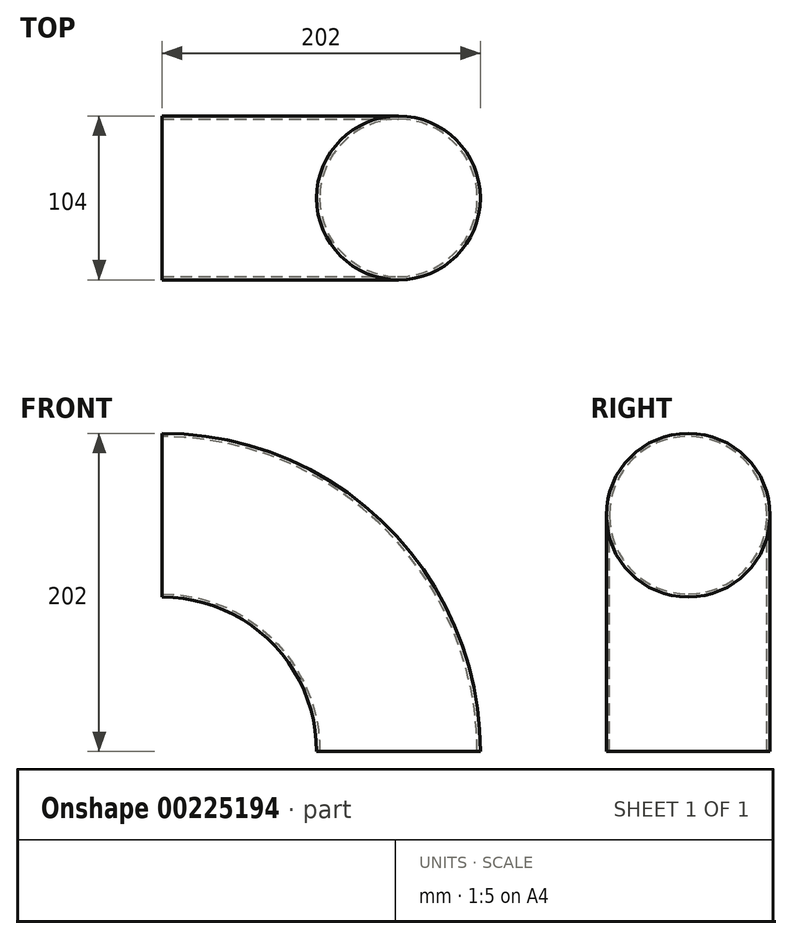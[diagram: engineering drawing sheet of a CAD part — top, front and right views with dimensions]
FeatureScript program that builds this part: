
annotation { "Feature Type Name" : "Feature", "Feature Type Description" : "" }
export const myFeature = defineFeature(function(context is Context, id is Id, definition is map)
    precondition{}
    {
        {
            var Q0;
            Q0=qCreatedBy(makeId("Right.planeOp"),FACE);
            var sketch = newSketch(context, id + "F0", { "sketchPlane" : qUnion([Q0])});
            skCircle(sketch, "E0", {"center": v(0, 0) * mm, "radius": 52 * mm});
            skCircle(sketch, "E1", {"center": v(0, 0) * mm, "radius": 50 * mm});
            skSolve(sketch);
        }
        {
            var Q0;
            Q0=qCreatedBy(makeId("Front.planeOp"),FACE);
            var sketch = newSketch(context, id + "F1", { "sketchPlane" : qUnion([Q0])});
            skLineSegment(sketch, "E2", {"start": v(0, 0) * mm, "end": v(0, 0) * mm});
            skLineSegment(sketch, "E3", {"start": v(150, -150) * mm, "end": v(150, -150) * mm});
            skPoint(sketch, "E4.visualSharp", {"position": v(150, 0) * mm});
            skArc(sketch, "E4.filletArc", {"start": v(150, -150) * mm, "mid": v(106.07, -43.93) * mm, "end": v(0, 0) * mm});
            skSolve(sketch);
        }
        {
            var Q0;
            Q0=makeQuery(id+"F0.imprint","IMPRINT",FACE,{"disambiguationData":[TD([[makeQuery(id+"F0.imprint","IMPRINT",EDGE,{"derivedFrom":sQuery(id+"F0.wireOp",EDGE,"E0")}),1.0]])]});
            var Q1;
            Q1=sQuery(id+"F1.wireOp",EDGE,"E4.filletArc");
            sweep(context, id + "F2", {"profiles" : qUnion([Q0]), "path" : qUnion([Q1])});
        }
    });
